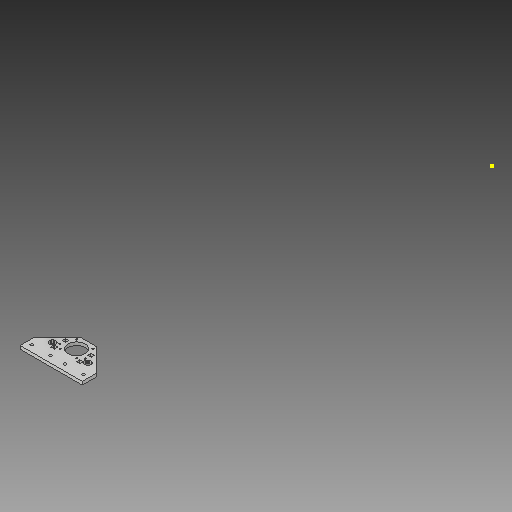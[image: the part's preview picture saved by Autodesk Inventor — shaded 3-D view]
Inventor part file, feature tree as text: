
AUTODESK INVENTOR PART (.ipt)
format: ipt  version: 2018 (Build 220112000, 112)  size: 766,976 bytes
history: native  units: mm
features: sketch x4, extrude x3, projected_geometry x1
ambient origin geometry x8: Origin, YZ Plane, XZ Plane, XY Plane, X Axis, Y Axis, Z Axis, Center Point
bodies: Solid1 (feature_tree)
feature tree (8):
  extrude  "Extrusion1"  Depth=6.0mm TaperAngle=0.0deg
  extrude  "Extrusion2"  Depth=12.0mm
  sketch  "Sketch3"  dims[d6=3.2mm d7=3.2mm]
  sketch  "Sketch4"  dims[d8=3.2mm d9=3.2mm d10=3.2mm d11=3.2mm d12=5.2mm d13=5.2mm d14=5.2mm d15=6.0mm d16=0.0mm]
  extrude  "Extrusion3"  Depth=3.2mm
  sketch  "Sketch1"  dims[d0=6.0mm d1=0.0mm d2=6.0mm d3=0.0mm]
  sketch  "Sketch2"  dims[d4=12.0mm d5=12.0mm]
  projected_geometry  "Projected Loop1"
